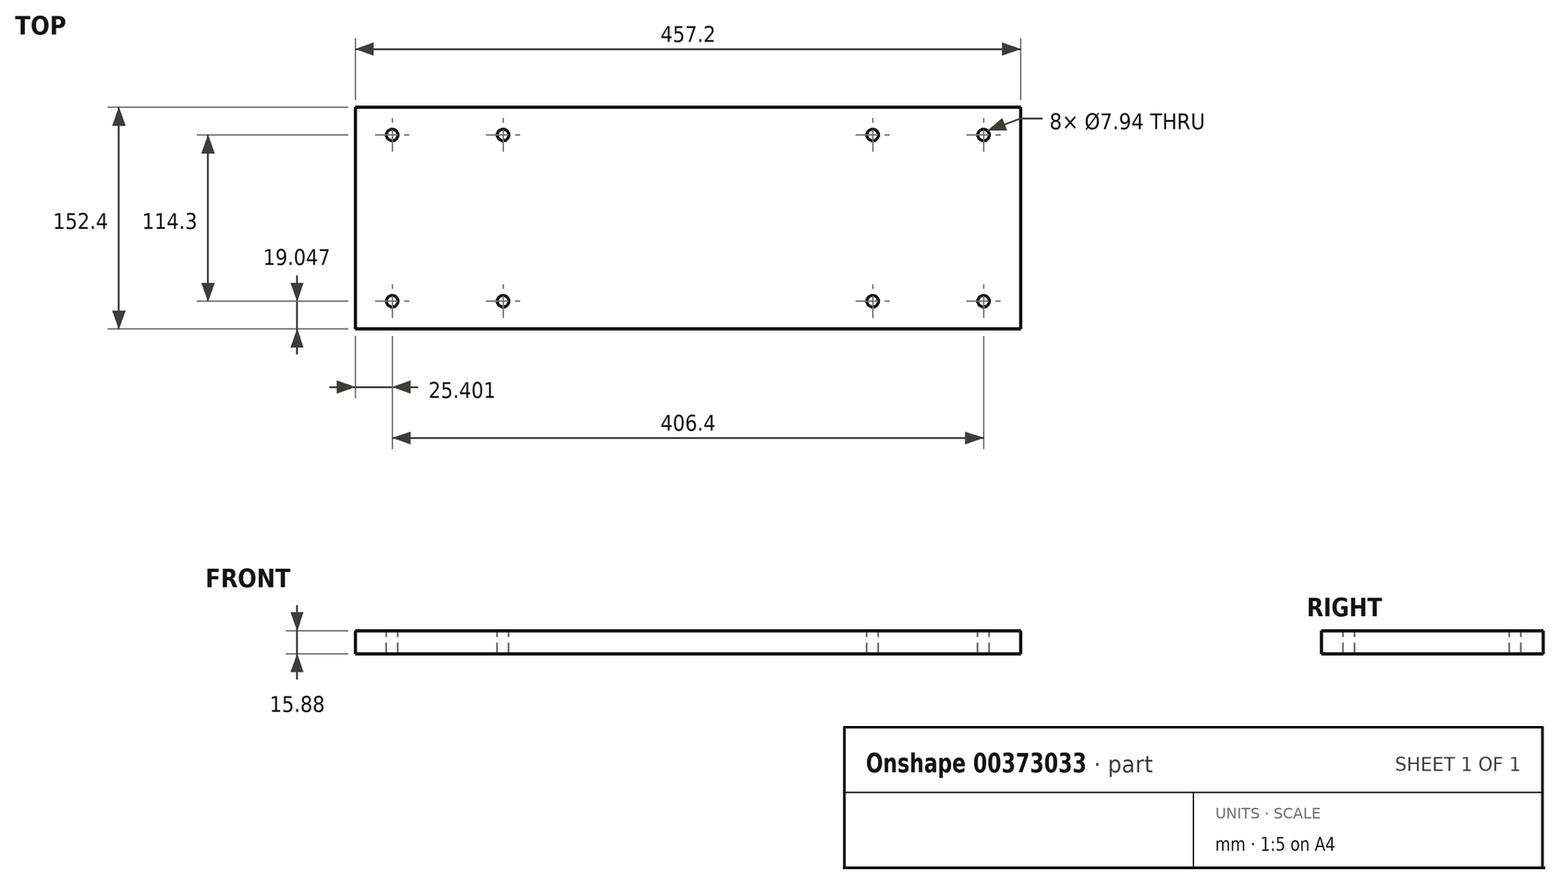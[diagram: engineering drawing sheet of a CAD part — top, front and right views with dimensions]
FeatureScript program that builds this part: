
annotation { "Feature Type Name" : "Feature", "Feature Type Description" : "" }
export const myFeature = defineFeature(function(context is Context, id is Id, definition is map)
    precondition{}
    {
        {
            var Q0;
            Q0=qCreatedBy(makeId("Top.planeOp"),FACE);
            var sketch = newSketch(context, id + "F0", { "sketchPlane" : qUnion([Q0])});
            skLineSegment(sketch, "E0.bottom", {"start": v(-171.26, 108.67) * mm, "end": v(285.94, 108.67) * mm});
            skLineSegment(sketch, "E0.top", {"start": v(-171.26, -43.73) * mm, "end": v(285.94, -43.73) * mm});
            skLineSegment(sketch, "E0.left", {"start": v(-171.26, 108.67) * mm, "end": v(-171.26, -43.73) * mm});
            skLineSegment(sketch, "E0.right", {"start": v(285.94, 108.67) * mm, "end": v(285.94, -43.73) * mm});
            skSolve(sketch);
        }
        {
            var Q0;
            Q0=makeQuery(id+"F0.imprint","IMPRINT",FACE,{"disambiguationData":[TD([[makeQuery(id+"F0.imprint","IMPRINT",EDGE,{"derivedFrom":sQuery(id+"F0.wireOp",EDGE,"E0.bottom")}),-1.0]])]});
            extrude(context, id + "F1", {"entities" : qUnion([Q0]), "depth" : 15.88 * mm, "offsetDistance" : 25.4 * mm});
        }
        {
            var Q0;
            Q0=makeQuery(id+"F1.opExtrude","CAP_FACE",FACE,{"disambiguationData":[OSD([sQuery(id+"F0.wireOp",EDGE,"E0.bottom"),sQuery(id+"F0.wireOp",EDGE,"E0.top"),sQuery(id+"F0.wireOp",EDGE,"E0.left"),sQuery(id+"F0.wireOp",EDGE,"E0.right")])],"isStart":false});
            var sketch = newSketch(context, id + "F2", { "sketchPlane" : qUnion([Q0])});
            skPoint(sketch, "E1", {"position": v(-145.86, 89.62) * mm});
            skPoint(sketch, "E2", {"position": v(-69.66, 89.62) * mm});
            skPoint(sketch, "E3", {"position": v(260.54, 89.62) * mm});
            skPoint(sketch, "E4", {"position": v(184.34, 89.62) * mm});
            skLineSegment(sketch, "E5", {"start": v(-171.26, 32.47) * mm, "end": v(285.94, 32.47) * mm});
            skPoint(sketch, "E6.MirrorP", {"position": v(-145.86, -24.68) * mm});
            skPoint(sketch, "E7.MirrorP", {"position": v(-69.66, -24.68) * mm});
            skPoint(sketch, "E8.MirrorP", {"position": v(184.34, -24.68) * mm});
            skPoint(sketch, "E9.MirrorP", {"position": v(260.54, -24.68) * mm});
            skSolve(sketch);
        }
        {
            var Q0;
            Q0=sQuery(id+"F2.wireOp",VERTEX,"E1");
            var Q1;
            Q1=sQuery(id+"F2.wireOp",VERTEX,"E2");
            var Q2;
            Q2=sQuery(id+"F2.wireOp",VERTEX,"E4");
            var Q3;
            Q3=sQuery(id+"F2.wireOp",VERTEX,"E3");
            var Q4;
            Q4=sQuery(id+"F2.wireOp",VERTEX,"E9.MirrorP");
            var Q5;
            Q5=sQuery(id+"F2.wireOp",VERTEX,"E8.MirrorP");
            var Q6;
            Q6=sQuery(id+"F2.wireOp",VERTEX,"E7.MirrorP");
            var Q7;
            Q7=sQuery(id+"F2.wireOp",VERTEX,"E6.MirrorP");
            var Q8;
            Q8=makeQuery(id+"F1.opExtrude","SWEPT_BODY",BODY,{"disambiguationData":[OSD([sQuery(id+"F0.wireOp",EDGE,"E0.bottom"),sQuery(id+"F0.wireOp",EDGE,"E0.top"),sQuery(id+"F0.wireOp",EDGE,"E0.left"),sQuery(id+"F0.wireOp",EDGE,"E0.right")])]});
            hole(context, id + "F3", {"style" : HoleStyle.SIMPLE, "endStyle" : HoleEndStyle.BLIND, "standardTappedOrClearance" : lookupTablePath({ "standard" : "ANSI", "engagement" : "75%", "pitch" : "16 tpi", "size" : "3/8", "type" : "Tapped" }), "standardBlindInLast" : lookupTablePath({ "standard" : "ANSI", "fit" : "Normal", "engagement" : "75%", "pitch" : "16 tpi", "size" : "3/8", "type" : "Clearance & tapped" }), "holeDiameter" : 7.94 * mm, "majorDiameter" : 9.52 * mm, "showTappedDepth" : true, "holeDepth" : 17.46 * mm, "tappedDepth" : 12.7 * mm, "tapClearance" : 3, "locations" : qUnion([Q0, Q1, Q2, Q3, Q4, Q5, Q6, Q7]), "scope" : qUnion([Q8])});
        }
    });
